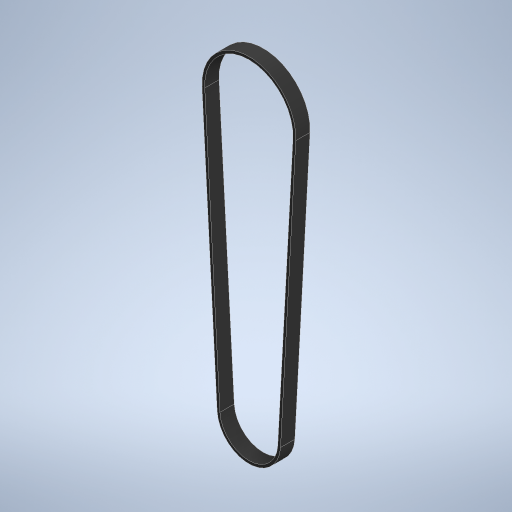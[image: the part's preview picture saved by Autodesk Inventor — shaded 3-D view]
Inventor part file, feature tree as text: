
AUTODESK INVENTOR PART (.ipt)
format: ipt  version: 2024 (Build 280153000, 153)  size: 254,976 bytes
history: native  units: in
note: dims shown in document units (in); Inventor stores cm internally (conversion verified against a paired STEP export)
features: extrude x1, sketch x1
ambient origin geometry x8: Origin, YZ Plane, XZ Plane, XY Plane, X Axis, Y Axis, Z Axis, Center Point
bodies: Solid1 (feature_tree)
feature tree (2):
  extrude  "Extrusion1"  Depth=0.3543in
  sketch  "Sketch1"  dims[d0=6.789in d1=1.504in d2=2.256in d3=0.0343in d4=0.0343in d5=0.3543in d6=0.0in]
